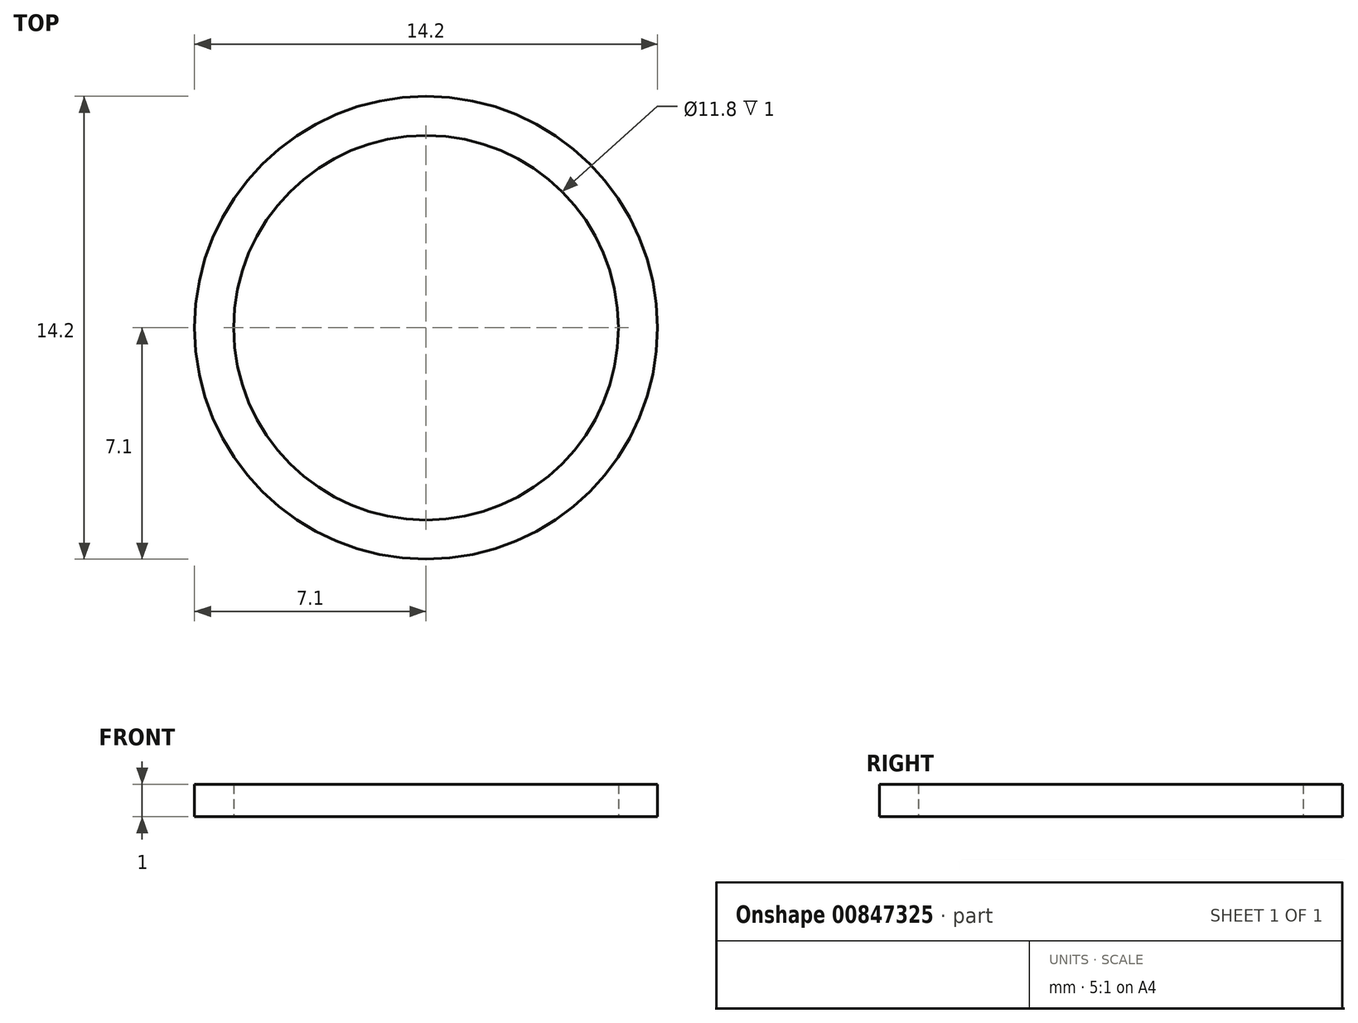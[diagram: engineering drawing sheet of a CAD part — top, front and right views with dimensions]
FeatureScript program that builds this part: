
annotation { "Feature Type Name" : "Feature", "Feature Type Description" : "" }
export const myFeature = defineFeature(function(context is Context, id is Id, definition is map)
    precondition{}
    {
        {
            var Q0;
            Q0=qCreatedBy(makeId("Top.planeOp"),FACE);
            var sketch = newSketch(context, id + "F0", { "sketchPlane" : qUnion([Q0])});
            skCircle(sketch, "E0", {"center": v(0, 0) * mm, "radius": 7.1 * mm});
            skCircle(sketch, "E1.0", {"center": v(0, 0) * mm, "radius": 5.9 * mm});
            skSolve(sketch);
        }
        {
            var Q0;
            Q0 = qSketchRegion(id + "F0", true);
            extrude(context, id + "F1", {"entities" : qUnion([Q0]), "depth" : 1 * mm, "offsetDistance" : 25 * mm});
        }
    });
